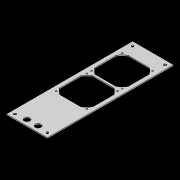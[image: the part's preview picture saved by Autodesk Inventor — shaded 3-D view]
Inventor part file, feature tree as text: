
AUTODESK INVENTOR PART (.ipt)
format: ipt  version: 2018.2 (Build 222227000, 227)  size: 220,160 bytes
history: native  units: mm
features: extrude x4, sketch x4, other x1
ambient origin geometry x8: Origin, YZ Plane, XZ Plane, XY Plane, X Axis, Y Axis, Z Axis, Center Point
bodies: Body1 (feature_tree)
feature tree (9):
  other  "ソリッド1"
  extrude  "押し出し1"  Depth=110.0mm
  extrude  "押し出し2"  Depth=340.0mm
  extrude  "押し出し3"  TaperAngle=135.0deg  [1 undecoded]
  extrude  "押し出し4"  Depth=30.0mm
  sketch  "スケッチ1"
  sketch  "スケッチ2"
  sketch  "スケッチ3"
  sketch  "スケッチ4"
note: 1 required parameter value undecoded (feature->parameter linkage not recoverable at this tier; creation-order binding heuristic only, values carry confidence <= 0.55)
